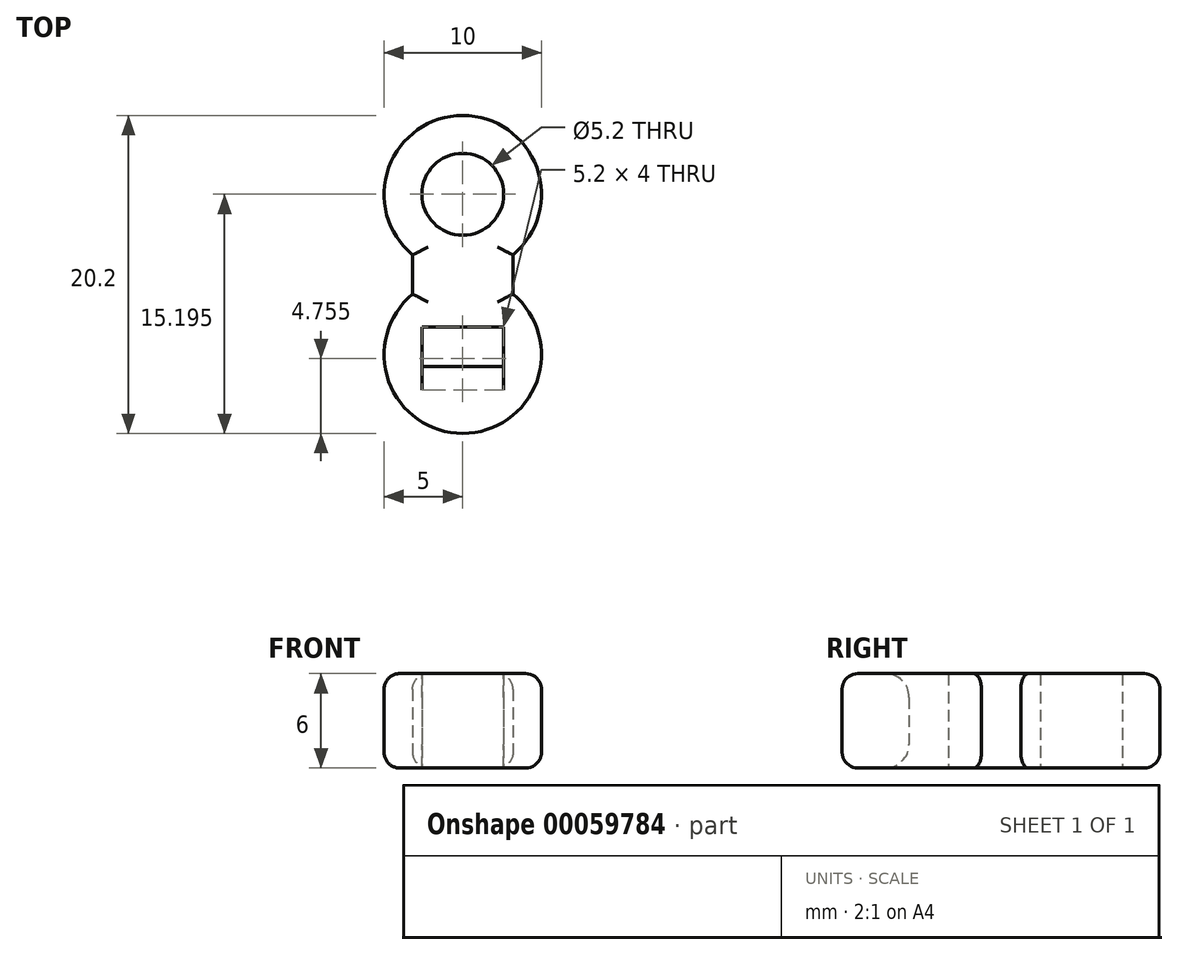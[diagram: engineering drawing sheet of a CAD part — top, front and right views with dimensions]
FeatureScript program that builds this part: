
annotation { "Feature Type Name" : "Feature", "Feature Type Description" : "" }
export const myFeature = defineFeature(function(context is Context, id is Id, definition is map)
    precondition{}
    {
        {
            var Q0;
            Q0=qCreatedBy(makeId("Top.planeOp"),FACE);
            var sketch = newSketch(context, id + "F0", { "sketchPlane" : qUnion([Q0])});
            skCircle(sketch, "E0", {"center": v(0, 5.1) * mm, "radius": 5 * mm});
            skCircle(sketch, "E1", {"center": v(0, -5.1) * mm, "radius": 5 * mm});
            skLineSegment(sketch, "E2", {"start": v(-3.2, 1.25) * mm, "end": v(-3.2, 0) * mm});
            skLineSegment(sketch, "E3", {"start": v(-3.2, 0) * mm, "end": v(-3.2, -1.25) * mm});
            skLineSegment(sketch, "E4", {"start": v(3.2, 1.25) * mm, "end": v(3.2, -1.25) * mm});
            skLineSegment(sketch, "E5", {"start": v(0, 0) * mm, "end": v(-3.2, 0) * mm});
            skLineSegment(sketch, "E6", {"start": v(0, 0) * mm, "end": v(3.2, 0) * mm});
            skCircle(sketch, "E7", {"center": v(0, 5.1) * mm, "radius": 2.6 * mm});
            skLineSegment(sketch, "E8.rect.bottom", {"start": v(-2.6, -3.35) * mm, "end": v(2.6, -3.35) * mm});
            skLineSegment(sketch, "E8.rect.top", {"start": v(-2.6, -5.85) * mm, "end": v(2.6, -5.85) * mm});
            skLineSegment(sketch, "E8.rect.left", {"start": v(-2.6, -3.35) * mm, "end": v(-2.6, -5.85) * mm});
            skLineSegment(sketch, "E8.rect.right", {"start": v(2.6, -3.35) * mm, "end": v(2.6, -5.85) * mm});
            skPoint(sketch, "E8.rect.middle", {"position": v(0, -4.6) * mm});
            skSolve(sketch);
        }
        {
            var Q0;
            Q0=qSketchRegion(id+"F0",true);
            extrude(context, id + "F1", {"entities" : qUnion([Q0]), "depth" : 6 * mm});
        }
        {
            var Q0;
            Q0=makeQuery(id+"F1.opExtrude","CAP_EDGE",EDGE,{"disambiguationData":[OSD([sQuery(id+"F0.wireOp",EDGE,"E8.rect.top")])],"isStart":false});
            var Q1;
            Q1=makeQuery(id+"F1.opExtrude","CAP_EDGE",EDGE,{"disambiguationData":[OSD([sQuery(id+"F0.wireOp",EDGE,"E8.rect.top")])],"isStart":true});
            fillet(context, id + "F2", {"entities" : qUnion([Q0, Q1]), "radius" : 1.5 * mm, "tangentPropagation" : true, "allowEdgeOverflow" : false});
        }
        {
            var Q0;
            Q0=makeQuery(id+"F1.opExtrude","CAP_EDGE",EDGE,{"disambiguationData":[OSD([sQuery(id+"F0.wireOp",EDGE,"E2"),sQuery(id+"F0.wireOp",EDGE,"E3")])],"isStart":false});
            var Q1;
            Q1=makeQuery(id+"F1.opExtrude","CAP_EDGE",EDGE,{"disambiguationData":[OSD([sQuery(id+"F0.wireOp",EDGE,"E0")])],"isStart":false});
            var Q2;
            Q2=makeQuery(id+"F1.opExtrude","CAP_EDGE",EDGE,{"disambiguationData":[OSD([sQuery(id+"F0.wireOp",EDGE,"E4")])],"isStart":false});
            var Q3;
            Q3=makeQuery(id+"F1.opExtrude","CAP_EDGE",EDGE,{"disambiguationData":[OSD([sQuery(id+"F0.wireOp",EDGE,"E1")])],"isStart":false});
            var Q4;
            Q4=makeQuery(id+"F1.opExtrude","CAP_EDGE",EDGE,{"disambiguationData":[OSD([sQuery(id+"F0.wireOp",EDGE,"E0")])],"isStart":true});
            var Q5;
            Q5=makeQuery(id+"F1.opExtrude","CAP_EDGE",EDGE,{"disambiguationData":[OSD([sQuery(id+"F0.wireOp",EDGE,"E4")])],"isStart":true});
            var Q6;
            Q6=makeQuery(id+"F1.opExtrude","CAP_EDGE",EDGE,{"disambiguationData":[OSD([sQuery(id+"F0.wireOp",EDGE,"E2"),sQuery(id+"F0.wireOp",EDGE,"E3")])],"isStart":true});
            var Q7;
            Q7=makeQuery(id+"F1.opExtrude","CAP_EDGE",EDGE,{"disambiguationData":[OSD([sQuery(id+"F0.wireOp",EDGE,"E1")])],"isStart":true});
            fillet(context, id + "F3", {"entities" : qUnion([Q0, Q1, Q2, Q3, Q4, Q5, Q6, Q7]), "radius" : 1 * mm, "tangentPropagation" : true, "allowEdgeOverflow" : false});
        }
    });
